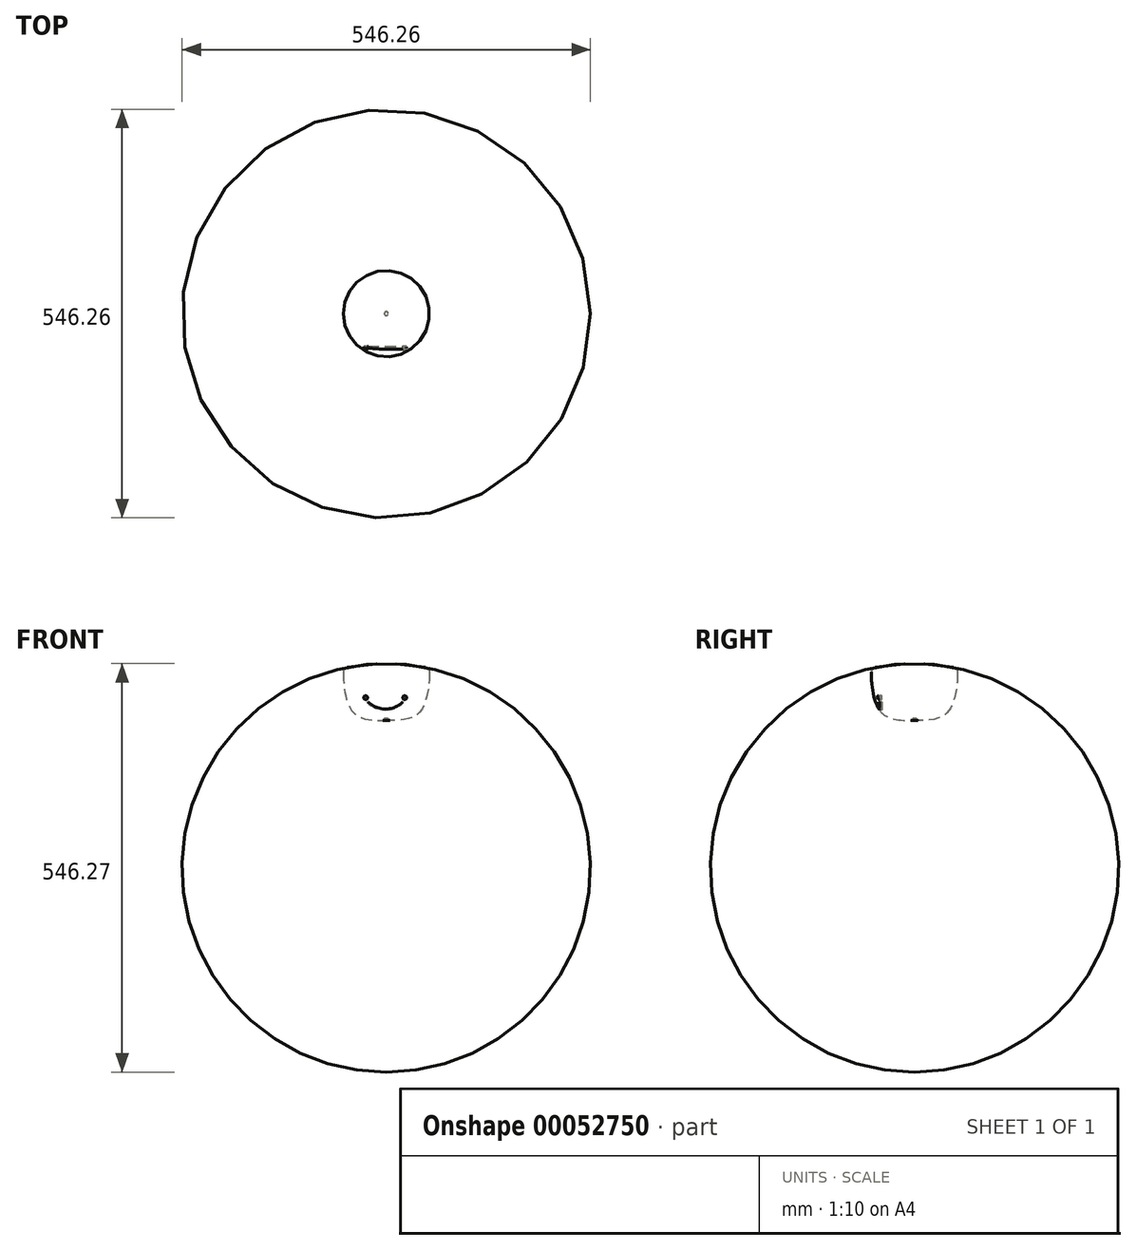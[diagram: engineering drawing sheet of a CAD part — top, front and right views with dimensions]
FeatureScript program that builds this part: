
annotation { "Feature Type Name" : "Feature", "Feature Type Description" : "" }
export const myFeature = defineFeature(function(context is Context, id is Id, definition is map)
    precondition{}
    {
        {
            var Q0;
            Q0=qCreatedBy(makeId("Front.planeOp"),FACE);
            var sketch = newSketch(context, id + "F0", { "sketchPlane" : qUnion([Q0])});
            skLineSegment(sketch, "E0", {"start": v(0, 0) * mm, "end": v(0, 50.8) * mm});
            skFitSpline(sketch, "E1", {"points": [v(38.1, 50.8) * mm, v(38.34, 38.11) * mm, v(35.07, 17.9) * mm, v(23.5, 3) * mm, v(0, 0) * mm], "startDerivative": vector(2.77, -59.25) * mm, "endDerivative": vector(-50.9, 0) * mm});
            skArc(sketch, "E2", {"start": v(34.9, 47.42) * mm, "mid": v(17.54, 49.95) * mm, "end": v(0, 50.8) * mm});
            skArc(sketch, "E3.filletArc", {"start": v(38.4, 43.26) * mm, "mid": v(37.4, 45.96) * mm, "end": v(34.9, 47.42) * mm});
            skLineSegment(sketch, "E4", {"start": v(0, 0) * mm, "end": v(3.18, 0) * mm});
            skSolve(sketch);
        }
        {
            var Q0;
            Q0 = qSketchRegion(id + "F0", true);
            var Q1;
            Q1=sQuery(id+"F0.wireOp",EDGE,"E0");
            revolve(context, id + "F1", {"entities" : qUnion([Q0]), "axis" : qUnion([Q1]), "revolveType" : RevolveType.FULL});
        }
        {
            var Q0;
            Q0=qCreatedBy(makeId("Front.planeOp"),FACE);
            cPlane(context, id + "F2", {"entities" : qUnion([Q0]), "cplaneType" : CPlaneType.OFFSET, "offset" : 50.8 * mm, "width" : 152.4 * mm, "height" : 152.4 * mm});
        }
        {
            var Q0;
            Q0=qCreatedBy(id+"F2.planeOp",FACE);
            var sketch = newSketch(context, id + "F3", { "sketchPlane" : qUnion([Q0])});
            skCircle(sketch, "E5", {"center": v(-18.39, 20.46) * mm, "radius": 1.71 * mm});
            skCircle(sketch, "E6", {"center": v(16.34, 20.46) * mm, "radius": 1.71 * mm});
            skArc(sketch, "E7", {"start": v(-16.37, 16.82) * mm, "mid": v(-0.97, 10.33) * mm, "end": v(14.54, 16.58) * mm});
            skArc(sketch, "E8.0", {"start": v(-16.9, 16.3) * mm, "mid": v(-0.97, 9.58) * mm, "end": v(15.06, 16.05) * mm});
            skLineSegment(sketch, "E9", {"start": v(-16.37, 16.82) * mm, "end": v(-16.9, 16.3) * mm});
            skLineSegment(sketch, "E10", {"start": v(14.54, 16.58) * mm, "end": v(15.06, 16.05) * mm});
            skSolve(sketch);
        }
        {
            var Q0;
            Q0 = qSketchRegion(id + "F3", true);
            extrude(context, id + "F4", {"entities" : qUnion([Q0]), "oppositeDirection" : true, "depth" : 21.59 * mm});
        }
        {
            var Q0;
            Q0=makeQuery(id+"F4.opExtrude","SWEPT_BODY",BODY,{"disambiguationData":[OSD([sQuery(id+"F3.wireOp",EDGE,"E5")])]});
            var Q1;
            Q1=makeQuery(id+"F4.opExtrude","SWEPT_BODY",BODY,{"disambiguationData":[OSD([sQuery(id+"F3.wireOp",EDGE,"E7"),sQuery(id+"F3.wireOp",EDGE,"E8.0"),sQuery(id+"F3.wireOp",EDGE,"E9"),sQuery(id+"F3.wireOp",EDGE,"E10")])]});
            var Q2;
            Q2=makeQuery(id+"F4.opExtrude","SWEPT_BODY",BODY,{"disambiguationData":[OSD([sQuery(id+"F3.wireOp",EDGE,"E6")])]});
            var Q3;
            Q3=makeQuery(id+"F1.opRevolve","SWEPT_BODY",BODY,{"disambiguationData":[OSD([sQuery(id+"F0.wireOp",EDGE,"E0"),sQuery(id+"F0.wireOp",EDGE,"2ab0945a-3d79-4475-b4e3-0925875c39e2"),sQuery(id+"F0.wireOp",EDGE,"52c6e8fe-6c53-4660-81ae-a93639e3b140")])]});
            booleanBodies(context, id + "F5", {"operationType" : BooleanOperationType.SUBTRACTION, "tools" : qUnion([Q0, Q1, Q2]), "targets" : qUnion([Q3])});
        }
        {
            var Q0;
            Q0=makeQuery(id+"F1.opRevolve","SWEPT_BODY",BODY,{"disambiguationData":[OSD([sQuery(id+"F0.wireOp",EDGE,"E0"),sQuery(id+"F0.wireOp",EDGE,"2ab0945a-3d79-4475-b4e3-0925875c39e2"),sQuery(id+"F0.wireOp",EDGE,"52c6e8fe-6c53-4660-81ae-a93639e3b140")])]});
            var Q1;
            Q1=qCreatedBy(makeId("Origin.pointOp"),VERTEX);
            transform(context, id + "F6", {"entities" : qUnion([Q0]), "transformType" : TransformType.SCALE_UNIFORMLY, "scale" : 1.5, "makeCopy" : false, "scalePoint" : qUnion([Q1])});
        }
        {
            var Q0;
            Q0=qCreatedBy(makeId("Top.planeOp"),FACE);
            var sketch = newSketch(context, id + "F7", { "sketchPlane" : qUnion([Q0])});
            skCircle(sketch, "E11", {"center": v(0, 0) * mm, "radius": 2.57 * mm});
            skSolve(sketch);
        }
        {
            var Q0;
            Q0 = qSketchRegion(id + "F7", true);
            extrude(context, id + "F8", {"entities" : qUnion([Q0]), "operationType" : NewBodyOperationType.REMOVE, "depth" : 2.54 * mm});
        }
    });
